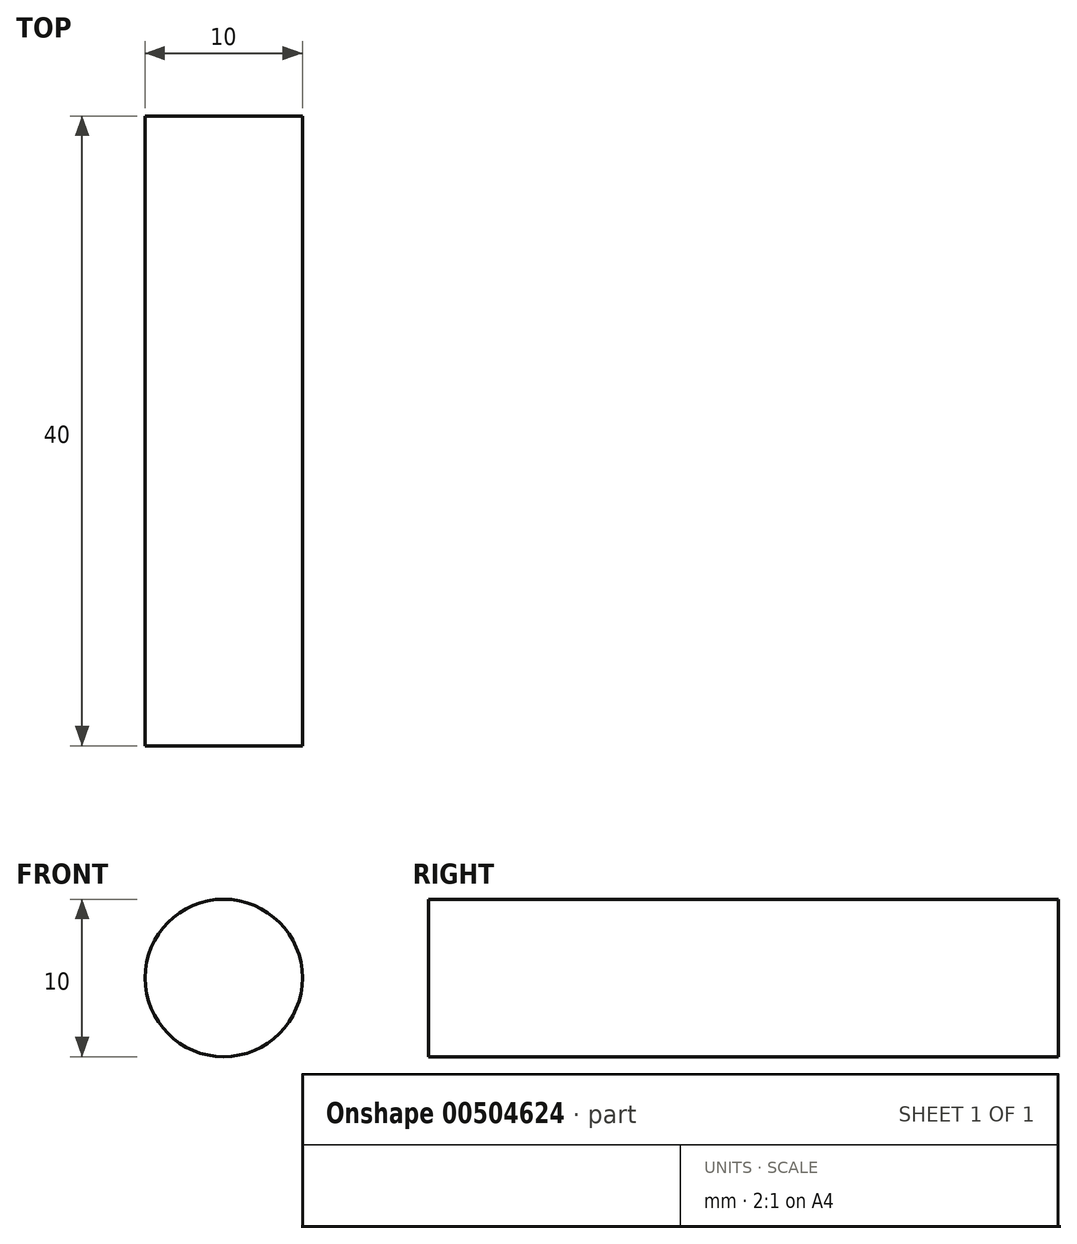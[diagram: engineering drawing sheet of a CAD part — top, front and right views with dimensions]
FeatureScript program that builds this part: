
annotation { "Feature Type Name" : "Feature", "Feature Type Description" : "" }
export const myFeature = defineFeature(function(context is Context, id is Id, definition is map)
    precondition{}
    {
        {
            var Q0;
            Q0=qCreatedBy(makeId("Front.planeOp"),FACE);
            var sketch = newSketch(context, id + "F0", { "sketchPlane" : qUnion([Q0])});
            skCircle(sketch, "E0", {"center": v(0, 0) * mm, "radius": 5 * mm});
            skLineSegment(sketch, "E1", {"start": v(0, 0) * mm, "end": v(5, 0) * mm});
            skSolve(sketch);
        }
        {
            var Q0;
            Q0=qSketchRegion(id+"F0",true);
            extrude(context, id + "F1", {"entities" : qUnion([Q0]), "depth" : 20 * mm, "hasSecondDirection" : true, "secondDirectionOppositeDirection" : true, "secondDirectionDepth" : 20 * mm, "offsetDistance" : 25 * mm});
        }
    });
